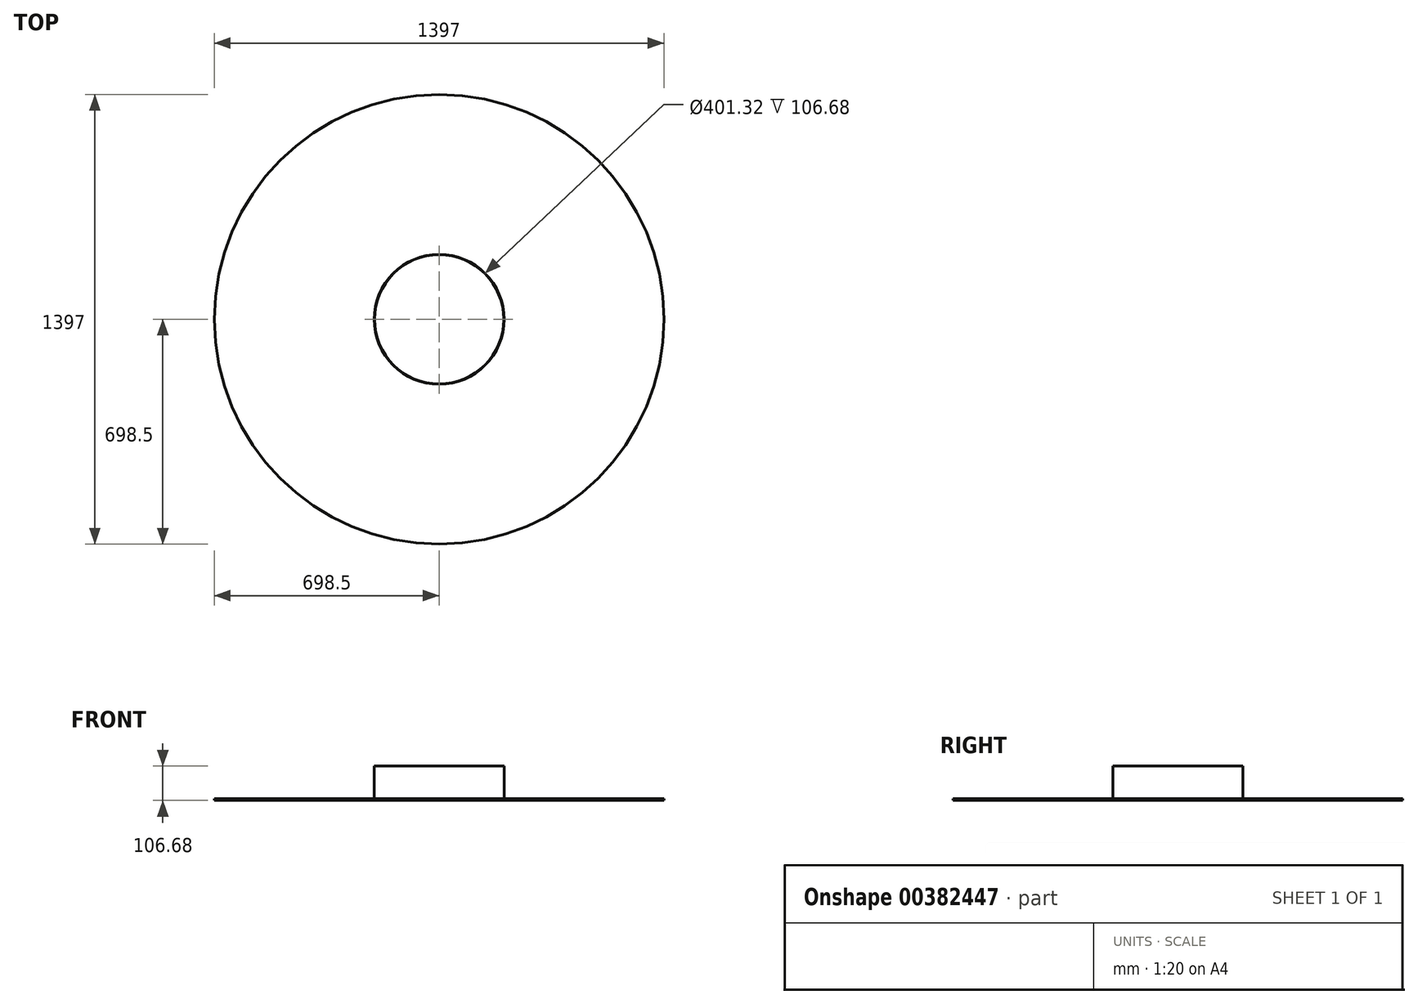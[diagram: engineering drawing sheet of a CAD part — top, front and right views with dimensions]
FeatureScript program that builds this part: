
annotation { "Feature Type Name" : "Feature", "Feature Type Description" : "" }
export const myFeature = defineFeature(function(context is Context, id is Id, definition is map)
    precondition{}
    {
        {
            var Q0;
            Q0=qCreatedBy(makeId("Top.planeOp"),FACE);
            var sketch = newSketch(context, id + "F0", { "sketchPlane" : qUnion([Q0])});
            skCircle(sketch, "E0", {"center": v(0, 0) * mm, "radius": 698.5 * mm});
            skCircle(sketch, "E1", {"center": v(0, 0) * mm, "radius": 200.66 * mm});
            skSolve(sketch);
        }
        {
            var Q0;
            Q0=makeQuery(id+"F0.imprint","IMPRINT",FACE,{"disambiguationData":[TD([[makeQuery(id+"F0.imprint","IMPRINT",EDGE,{"derivedFrom":sQuery(id+"F0.wireOp",EDGE,"E0")}),1.0]])]});
            extrude(context, id + "F1", {"entities" : qUnion([Q0]), "oppositeDirection" : true, "depth" : 5.08 * mm});
        }
        {
            var Q0;
            Q0=makeQuery(id+"F0.imprint","IMPRINT",FACE,{"disambiguationData":[TD([[makeQuery(id+"F0.imprint","IMPRINT",EDGE,{"derivedFrom":sQuery(id+"F0.wireOp",EDGE,"E1")}),1.0]])]});
            var sketch = newSketch(context, id + "F2", { "sketchPlane" : qUnion([Q0])});
            skCircle(sketch, "E2", {"center": v(0, 0) * mm, "radius": 200.66 * mm});
            skCircle(sketch, "E3", {"center": v(0, 0) * mm, "radius": 201.93 * mm});
            skSolve(sketch);
        }
        {
            var Q0;
            Q0 = qSketchRegion(id + "F2", true);
            extrude(context, id + "F3", {"entities" : qUnion([Q0]), "operationType" : NewBodyOperationType.ADD, "depth" : 101.6 * mm});
        }
    });
